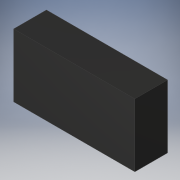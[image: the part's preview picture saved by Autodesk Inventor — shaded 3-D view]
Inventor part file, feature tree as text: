
AUTODESK INVENTOR PART (.ipt)
format: ipt  version: 2019 (Build 230136000, 136)  size: 120,832 bytes
history: native  units: mm
features: extrude x2, sketch x2, projected_geometry x1
ambient origin geometry x8: Origin, YZ Plane, XZ Plane, XY Plane, X Axis, Y Axis, Z Axis, Center Point
bodies: Solid1 (feature_tree), Body1 (feature_tree)
feature tree (5):
  extrude  "Extrusion2"  Depth=12.5mm
  extrude  "Extrusion3"  Depth=8.0mm
  sketch  "Sketch2"  dims[d2=15.0mm d3=0.0mm d4=12.5mm]
  projected_geometry  "Projected Loop2"
  sketch  "Sketch3"  dims[d5=3.0mm d6=8.0mm d7=1.0mm d8=0.0mm]
